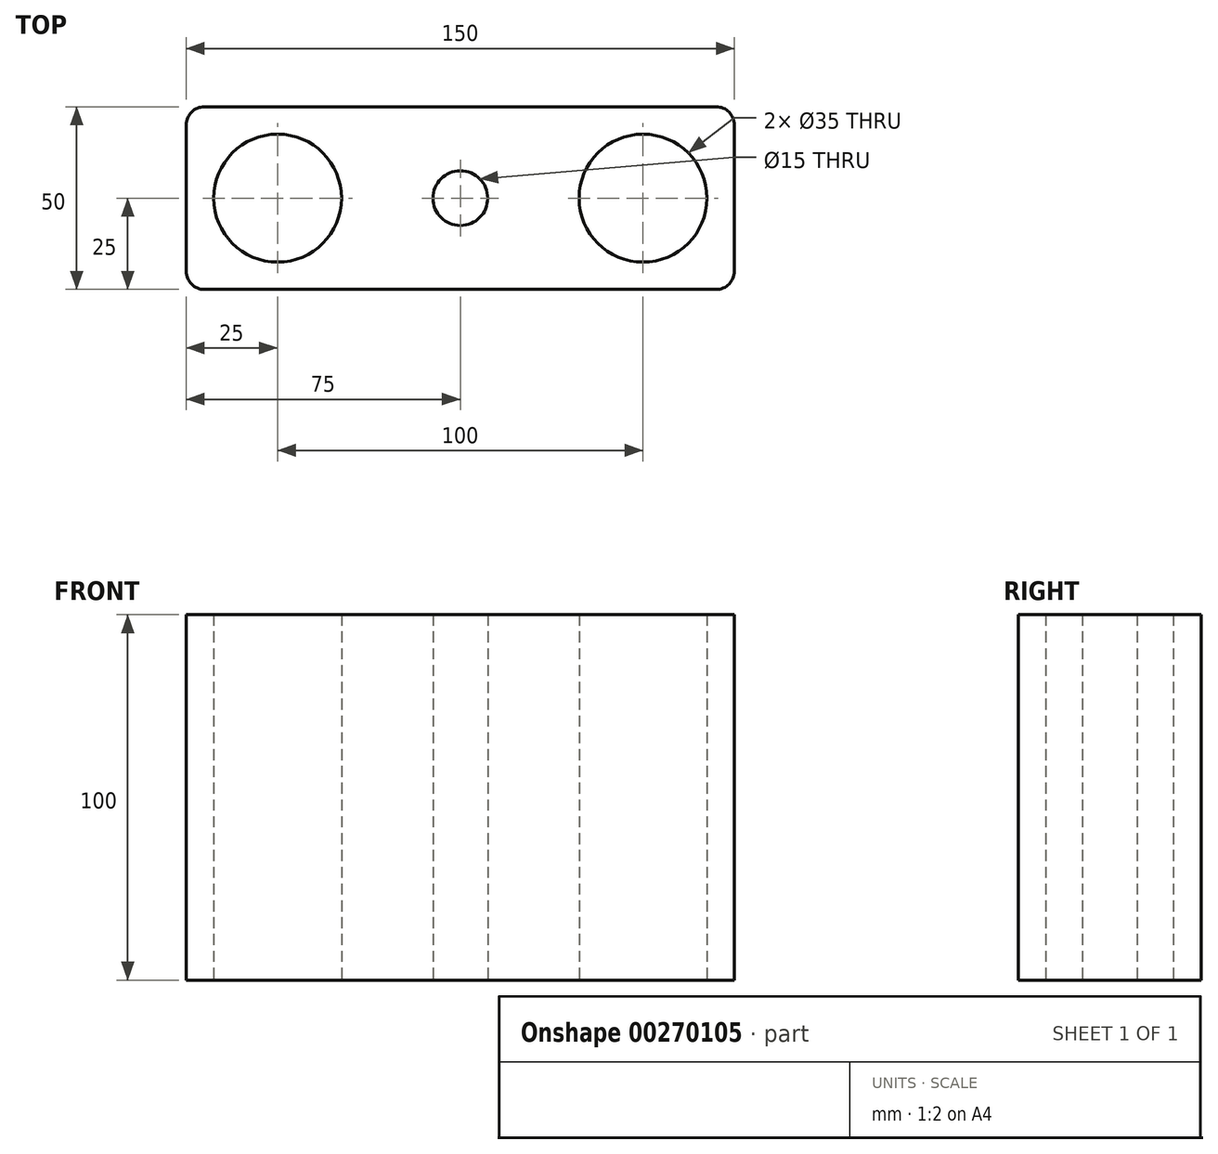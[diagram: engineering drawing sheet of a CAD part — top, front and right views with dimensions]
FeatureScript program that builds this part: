
annotation { "Feature Type Name" : "Feature", "Feature Type Description" : "" }
export const myFeature = defineFeature(function(context is Context, id is Id, definition is map)
    precondition{}
    {
        {
            var Q0;
            Q0=qCreatedBy(makeId("Top.planeOp"),FACE);
            var sketch = newSketch(context, id + "F0", { "sketchPlane" : qUnion([Q0])});
            skLineSegment(sketch, "E0.bottom", {"start": v(75, -25) * mm, "end": v(-75, -25) * mm});
            skLineSegment(sketch, "E0.top", {"start": v(75, 25) * mm, "end": v(-75, 25) * mm});
            skLineSegment(sketch, "E0.left", {"start": v(75, -25) * mm, "end": v(75, 25) * mm});
            skLineSegment(sketch, "E0.right", {"start": v(-75, -25) * mm, "end": v(-75, 25) * mm});
            skPoint(sketch, "E0.middle", {"position": v(0, 0) * mm});
            skPoint(sketch, "E1", {"position": v(-50, 0) * mm});
            skPoint(sketch, "E2", {"position": v(50, 0) * mm});
            skCircle(sketch, "E3", {"center": v(50, 0) * mm, "radius": 17.5 * mm});
            skCircle(sketch, "E4", {"center": v(-50, 0) * mm, "radius": 17.5 * mm});
            skCircle(sketch, "E5", {"center": v(0, 0) * mm, "radius": 7.5 * mm});
            skSolve(sketch);
        }
        {
            var Q0;
            Q0=makeQuery(id+"F0.imprint","IMPRINT",FACE,{"disambiguationData":[TD([[makeQuery(id+"F0.imprint","IMPRINT",EDGE,{"derivedFrom":sQuery(id+"F0.wireOp",EDGE,"E0.bottom")}),-1.0]])]});
            extrude(context, id + "F1", {"entities" : qUnion([Q0]), "depth" : 100 * mm});
        }
        {
            var Q0;
            Q0=makeQuery(id+"F1.opExtrude","SWEPT_EDGE",EDGE,{"disambiguationData":[OSD([sQuery(id+"F0.wireOp",EDGE,"E0.bottom"),sQuery(id+"F0.wireOp",EDGE,"E0.right")])]});
            var Q1;
            Q1=makeQuery(id+"F1.opExtrude","SWEPT_EDGE",EDGE,{"disambiguationData":[OSD([sQuery(id+"F0.wireOp",EDGE,"E0.bottom"),sQuery(id+"F0.wireOp",EDGE,"E0.left")])]});
            var Q2;
            Q2=makeQuery(id+"F1.opExtrude","SWEPT_EDGE",EDGE,{"disambiguationData":[OSD([sQuery(id+"F0.wireOp",EDGE,"E0.top"),sQuery(id+"F0.wireOp",EDGE,"E0.left")])]});
            var Q3;
            Q3=makeQuery(id+"F1.opExtrude","SWEPT_EDGE",EDGE,{"disambiguationData":[OSD([sQuery(id+"F0.wireOp",EDGE,"E0.top"),sQuery(id+"F0.wireOp",EDGE,"E0.right")])]});
            fillet(context, id + "F2", {"entities" : qUnion([Q0, Q1, Q2, Q3]), "radius" : 5 * mm, "tangentPropagation" : true, "allowEdgeOverflow" : false});
        }
    });
